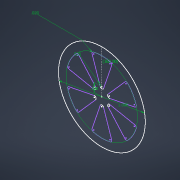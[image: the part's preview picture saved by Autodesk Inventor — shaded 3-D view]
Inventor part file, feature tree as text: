
AUTODESK INVENTOR PART (.ipt)
format: ipt  version: 2022 (Build 260153000, 153)  size: 104,960 bytes
history: native  units: in
note: dims shown in document units (in); Inventor stores cm internally (conversion verified against a paired STEP export)
features: sketch x1
ambient origin geometry x8: Origin, YZ Plane, XZ Plane, XY Plane, X Axis, Y Axis, Z Axis, Center Point
feature tree (1):
  sketch  "Sketch1"  dims[d0=1.0in d1=0.02in d2=0.02in d3=0.1in d4=2.3622in d6=360.0deg]
